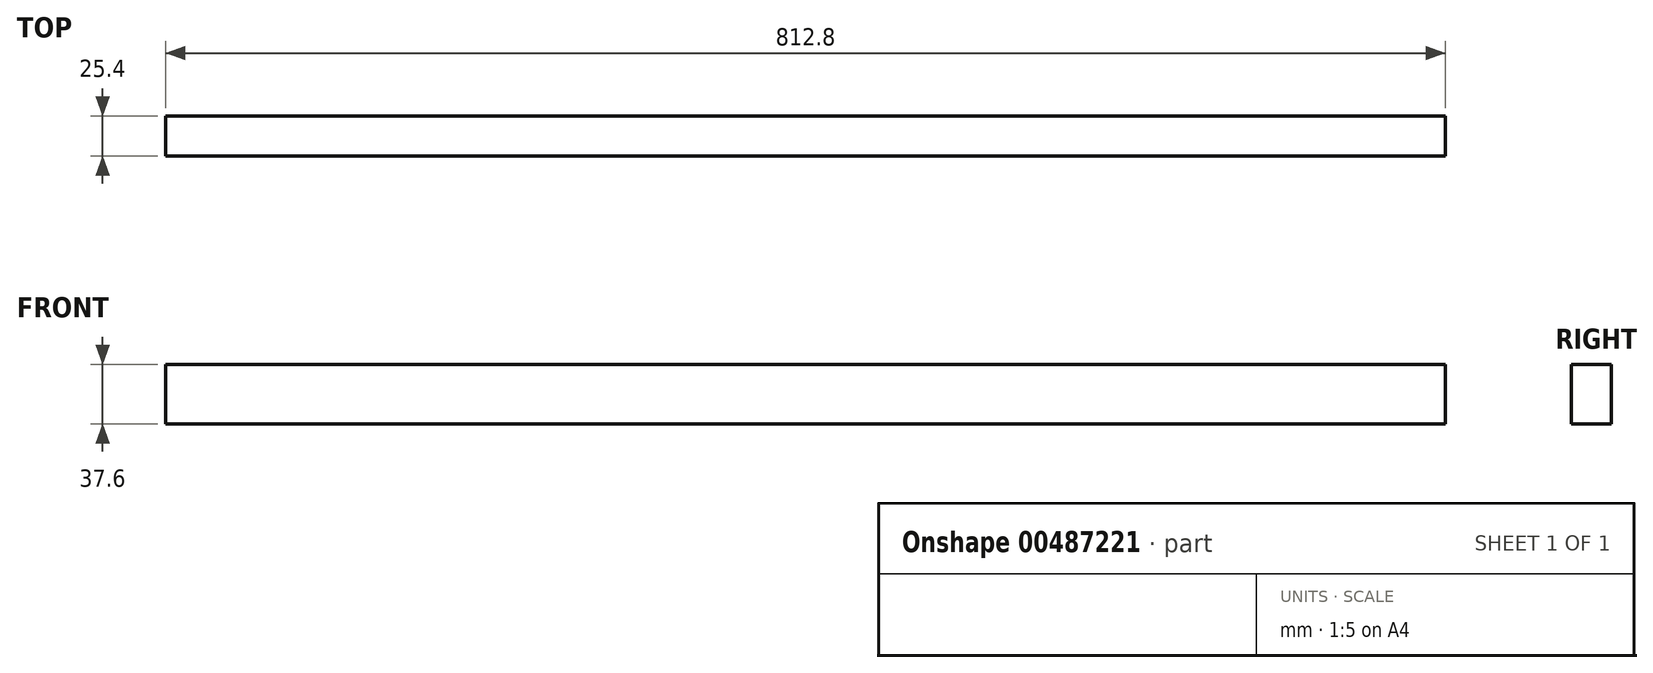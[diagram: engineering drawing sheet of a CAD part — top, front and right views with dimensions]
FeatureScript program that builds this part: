
annotation { "Feature Type Name" : "Feature", "Feature Type Description" : "" }
export const myFeature = defineFeature(function(context is Context, id is Id, definition is map)
    precondition{}
    {
        {
            var Q0;
            Q0=qCreatedBy(makeId("Front.planeOp"),FACE);
            var sketch = newSketch(context, id + "F0", { "sketchPlane" : qUnion([Q0])});
            skLineSegment(sketch, "E0.bottom", {"start": v(-406.4, -18.8) * mm, "end": v(406.4, -18.8) * mm});
            skLineSegment(sketch, "E0.top", {"start": v(-406.4, 18.8) * mm, "end": v(406.4, 18.8) * mm});
            skLineSegment(sketch, "E0.left", {"start": v(-406.4, -18.8) * mm, "end": v(-406.4, 18.8) * mm});
            skLineSegment(sketch, "E0.right", {"start": v(406.4, -18.8) * mm, "end": v(406.4, 18.8) * mm});
            skPoint(sketch, "E0.middle", {"position": v(0, 0) * mm});
            skSolve(sketch);
        }
        {
            var Q0;
            Q0 = qSketchRegion(id + "F0", true);
            extrude(context, id + "F1", {"entities" : qUnion([Q0]), "depth" : 25.4 * mm});
        }
    });
